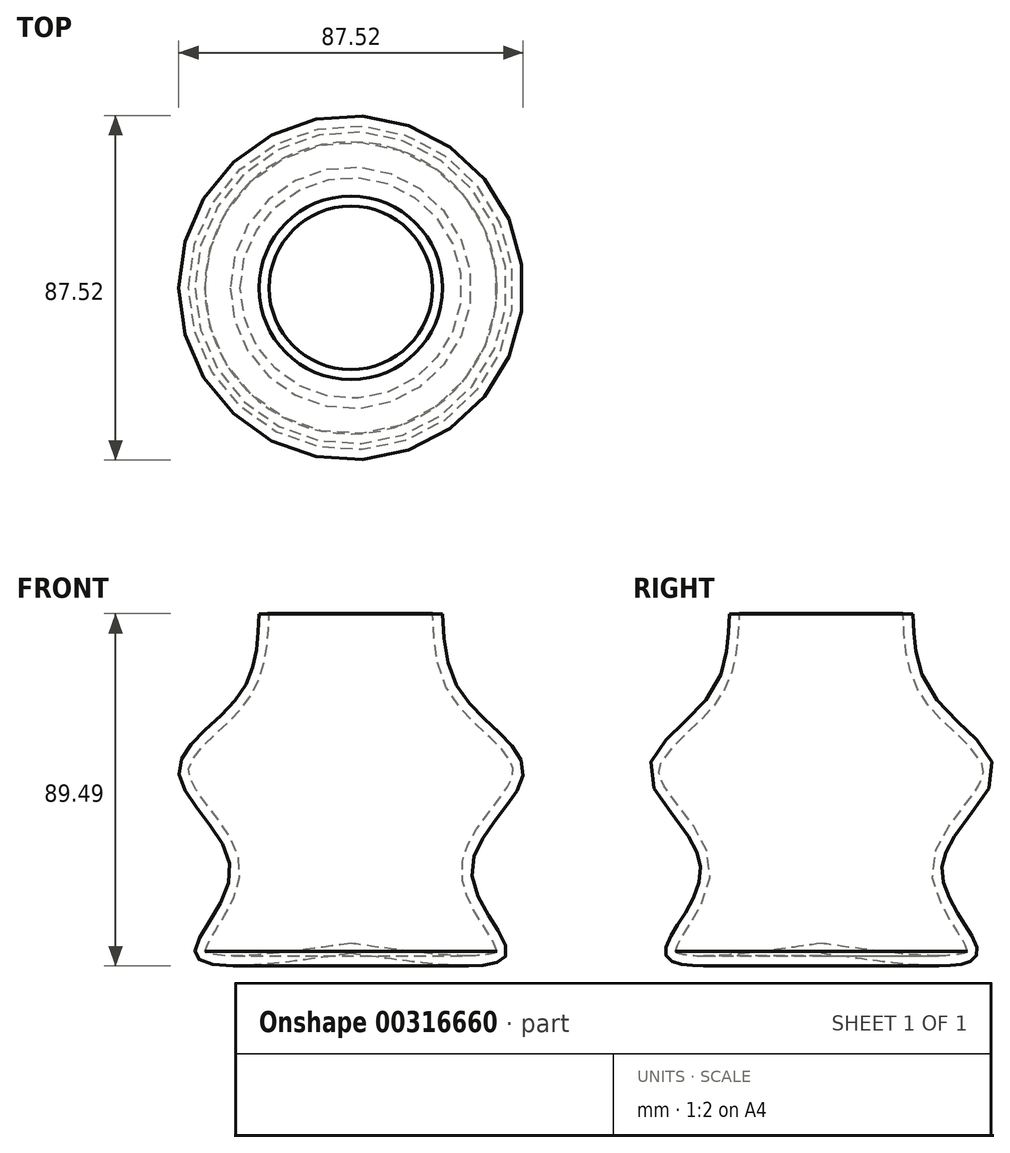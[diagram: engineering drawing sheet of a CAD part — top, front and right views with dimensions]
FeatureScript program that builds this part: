
annotation { "Feature Type Name" : "Feature", "Feature Type Description" : "" }
export const myFeature = defineFeature(function(context is Context, id is Id, definition is map)
    precondition{}
    {
        {
            var Q0;
            Q0=qCreatedBy(makeId("Front.planeOp"),FACE);
            var sketch = newSketch(context, id + "F0", { "sketchPlane" : qUnion([Q0])});
            skLineSegment(sketch, "E0", {"start": v(0, 0) * mm, "end": v(0, 87.5) * mm, "construction": true});
            skFitSpline(sketch, "E1", {"points": [v(0, 0) * mm, v(-39.6, 0) * mm, v(-30.66, 21.4) * mm, v(-43.75, 45.98) * mm, v(-28.74, 65.15) * mm, v(-23.31, 86.22) * mm], "startDerivative": vector(-239.05, -33.68) * mm, "endDerivative": vector(4.84, 122.69) * mm});
            skLineSegment(sketch, "E2", {"start": v(-23.31, 86.22) * mm, "end": v(2.24, 87.5) * mm});
            skLineSegment(sketch, "E3", {"start": v(0, 87.5) * mm, "end": v(0, 0) * mm});
            skSolve(sketch);
        }
        {
            var Q0;
            Q0 = qSketchRegion(id + "F0", true);
            var Q1;
            Q1=sQuery(id+"F0.wireOp",EDGE,"E0");
            revolve(context, id + "F1", {"entities" : qUnion([Q0]), "axis" : qUnion([Q1]), "revolveType" : RevolveType.FULL});
        }
        {
            var Q0;
            Q0=makeQuery(id+"F1.opRevolve","SWEPT_FACE",FACE,{"disambiguationData":[OSD([sQuery(id+"F0.wireOp",EDGE,"E2")])]});
            shell(context, id + "F2", {"entities" : qUnion([Q0]), "thickness" : 2.54 * mm});
        }
    });
